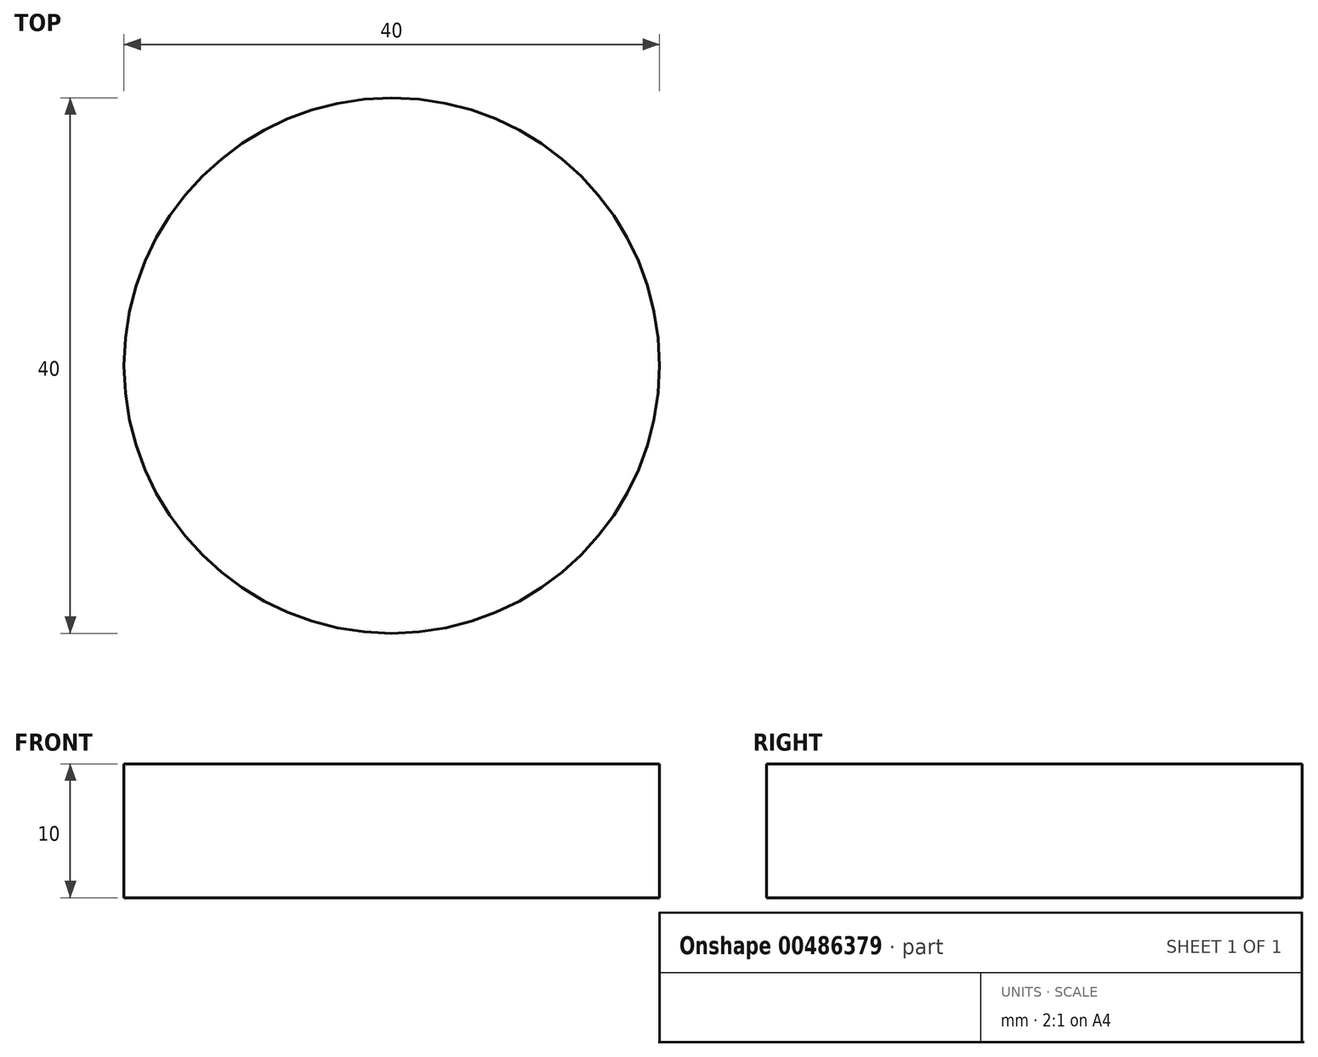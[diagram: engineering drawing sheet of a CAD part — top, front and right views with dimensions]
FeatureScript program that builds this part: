
annotation { "Feature Type Name" : "Feature", "Feature Type Description" : "" }
export const myFeature = defineFeature(function(context is Context, id is Id, definition is map)
    precondition{}
    {
        {
            var Q0;
            Q0=qCreatedBy(makeId("Top.planeOp"),FACE);
            var sketch = newSketch(context, id + "F0", { "sketchPlane" : qUnion([Q0])});
            skLineSegment(sketch, "E0.bottom", {"start": v(-20, 20) * mm, "end": v(20, 20) * mm});
            skLineSegment(sketch, "E0.top", {"start": v(-20, -20) * mm, "end": v(20, -20) * mm});
            skLineSegment(sketch, "E0.left", {"start": v(-20, 20) * mm, "end": v(-20, -20) * mm});
            skLineSegment(sketch, "E0.right", {"start": v(20, 20) * mm, "end": v(20, -20) * mm});
            skPoint(sketch, "E0.middle", {"position": v(0, 0) * mm});
            skCircle(sketch, "E1", {"center": v(0, 0) * mm, "radius": 20 * mm});
            skPoint(sketch, "E1.first.point", {"position": v(0, 20) * mm});
            skPoint(sketch, "E1.second.point", {"position": v(-20, 0) * mm});
            skPoint(sketch, "E1.third.point", {"position": v(0, -20) * mm});
            skSolve(sketch);
        }
        {
            var Q0;
            {var subQ0=sQuery(id+"F0.wireOp",EDGE,"E1");var subQ1=makeQuery(id+"F0.imprint","INTERSECT",VERTEX,{"derivedFrom":[sQuery(id+"F0.wireOp",EDGE,"E0.bottom"),subQ0]});Q0=makeQuery(id+"F0.imprint","IMPRINT",FACE,{"disambiguationData":[TD([[makeQuery(id+"F0.imprint","IMPRINT",EDGE,{"disambiguationData":[TD([[subQ1,1.0]])],"derivedFrom":subQ0}),1.0]])]});}
            extrude(context, id + "F1", {"entities" : qUnion([Q0]), "depth" : 10 * mm});
        }
    });
